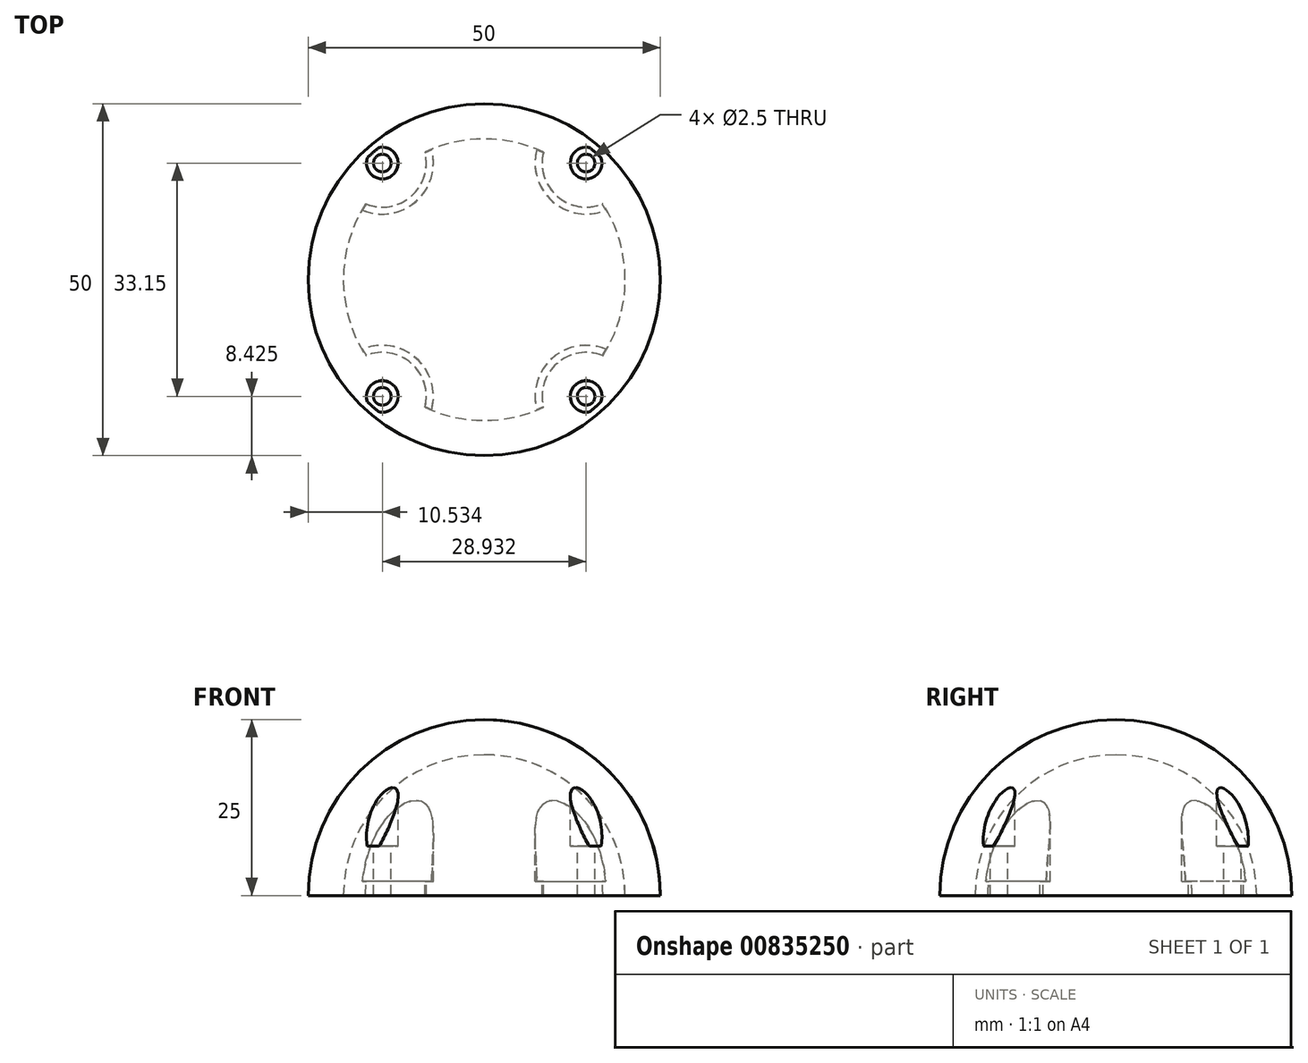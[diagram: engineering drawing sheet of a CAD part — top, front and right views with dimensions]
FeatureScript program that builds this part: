
annotation { "Feature Type Name" : "Feature", "Feature Type Description" : "" }
export const myFeature = defineFeature(function(context is Context, id is Id, definition is map)
    precondition{}
    {
        {
            var Q0;
            Q0=qCreatedBy(makeId("Top.planeOp"),FACE);
            var sketch = newSketch(context, id + "F0", { "sketchPlane" : qUnion([Q0])});
            skCircle(sketch, "E0", {"center": v(0, 0) * mm, "radius": 25 * mm});
            skSolve(sketch);
        }
        {
            var Q0;
            Q0=makeQuery(id+"F0.imprint","IMPRINT",FACE,{"disambiguationData":[TD([[makeQuery(id+"F0.imprint","IMPRINT",EDGE,{"derivedFrom":sQuery(id+"F0.wireOp",EDGE,"E0")}),1.0]])]});
            extrude(context, id + "F1", {"entities" : qUnion([Q0]), "depth" : 25 * mm, "offsetDistance" : 25 * mm});
        }
        {
            var Q0;
            Q0=makeQuery(id+"F1.opExtrude","CAP_FACE",FACE,{"disambiguationData":[OSD([sQuery(id+"F0.wireOp",EDGE,"E0")])],"isStart":false});
            var sketch = newSketch(context, id + "F2", { "sketchPlane" : qUnion([Q0])});
            skCircle(sketch, "E1", {"center": v(-14.47, -16.57) * mm, "radius": 3 * mm});
            skPoint(sketch, "E1.first.point", {"position": v(-16.44, -18.84) * mm});
            skPoint(sketch, "E1.second.point", {"position": v(-12.8, -14.08) * mm});
            skPoint(sketch, "E1.third.point", {"position": v(-15.23, -13.67) * mm});
            skCircle(sketch, "E2", {"center": v(-14.47, -16.57) * mm, "radius": 1.25 * mm});
            skCircle(sketch, "E3.MirrorC", {"center": v(-14.47, 16.57) * mm, "radius": 1.25 * mm});
            skCircle(sketch, "E4.MirrorC", {"center": v(-14.47, 16.57) * mm, "radius": 3 * mm});
            skCircle(sketch, "E5.MirrorC", {"center": v(14.47, -16.57) * mm, "radius": 1.25 * mm});
            skCircle(sketch, "E6.MirrorC", {"center": v(14.47, -16.57) * mm, "radius": 3 * mm});
            skCircle(sketch, "E7.MirrorC", {"center": v(14.47, 16.57) * mm, "radius": 3 * mm});
            skCircle(sketch, "E8.MirrorC", {"center": v(14.47, 16.57) * mm, "radius": 1.25 * mm});
            skSolve(sketch);
        }
        {
            var Q0;
            Q0=sQuery(id+"F2.wireOp",VERTEX,"E7.MirrorC.center");
            var Q1;
            Q1=sQuery(id+"F2.wireOp",VERTEX,"E5.MirrorC.center");
            var Q2;
            Q2=sQuery(id+"F2.wireOp",VERTEX,"E1.center");
            var Q3;
            Q3=sQuery(id+"F2.wireOp",VERTEX,"E3.MirrorC.center");
            var Q4;
            Q4=makeQuery(id+"F1.opExtrude","SWEPT_BODY",BODY,{"disambiguationData":[OSD([sQuery(id+"F0.wireOp",EDGE,"E0")])]});
            hole(context, id + "F3", {"style" : HoleStyle.C_BORE, "endStyle" : HoleEndStyle.THROUGH, "holeDiameter" : 2.5 * mm, "cBoreDiameter" : 4.5 * mm, "cBoreDepth" : 18 * mm, "majorDiameter" : 5 * mm, "isTappedThrough" : true, "tappedDepth" : 12 * mm, "tapClearance" : 3, "locations" : qUnion([Q0, Q1, Q2, Q3]), "scope" : qUnion([Q4])});
        }
        {
            var Q0;
            Q0=makeQuery(id+"F1.opExtrude","CAP_EDGE",EDGE,{"disambiguationData":[OSD([sQuery(id+"F0.wireOp",EDGE,"E0")])],"isStart":false});
            fillet(context, id + "F4", {"entities" : qUnion([Q0]), "radius" : 25 * mm, "tangentPropagation" : true, "allowEdgeOverflow" : false});
        }
        {
            var Q0;
            Q0=makeQuery(id+"F1.opExtrude","CAP_FACE",FACE,{"disambiguationData":[OSD([sQuery(id+"F0.wireOp",EDGE,"E0")])],"isStart":true});
            shell(context, id + "F5", {"entities" : qUnion([Q0]), "thickness" : 5 * mm});
        }
    });
